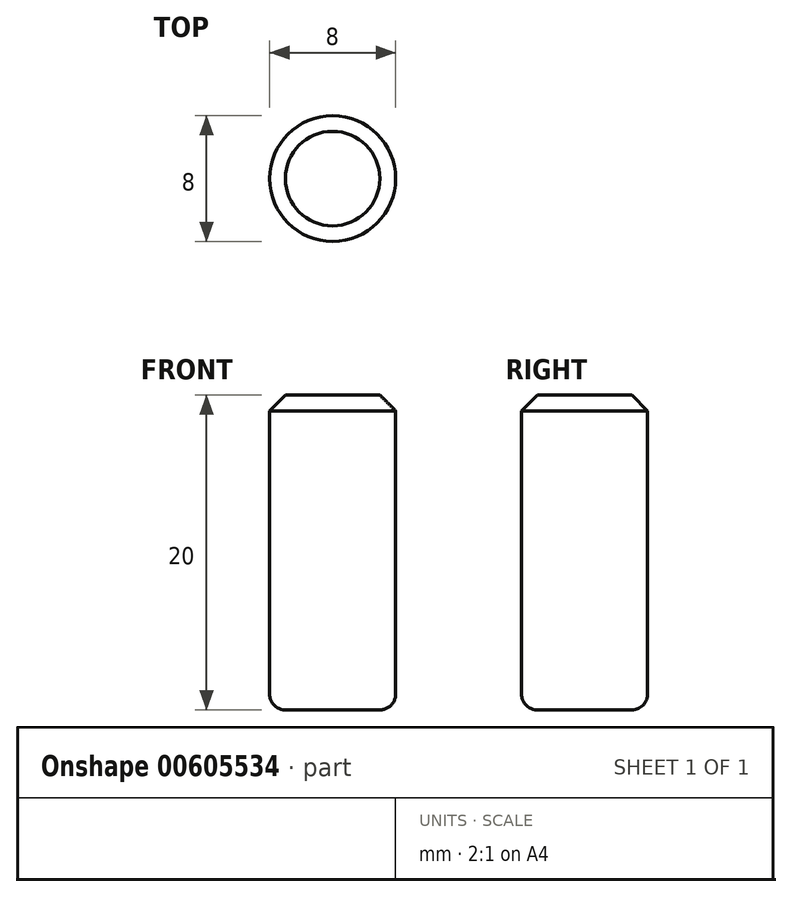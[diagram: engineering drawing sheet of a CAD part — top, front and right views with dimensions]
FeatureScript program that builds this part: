
annotation { "Feature Type Name" : "Feature", "Feature Type Description" : "" }
export const myFeature = defineFeature(function(context is Context, id is Id, definition is map)
    precondition{}
    {
        {
            var Q0;
            Q0=qCreatedBy(makeId("Top.planeOp"),FACE);
            var sketch = newSketch(context, id + "F0", { "sketchPlane" : qUnion([Q0])});
            skCircle(sketch, "E0", {"center": v(0, 0) * mm, "radius": 4 * mm});
            skSolve(sketch);
        }
        {
            var Q0;
            Q0=makeQuery(id+"F0.imprint","IMPRINT",FACE,{"disambiguationData":[TD([[makeQuery(id+"F0.imprint","IMPRINT",EDGE,{"derivedFrom":sQuery(id+"F0.wireOp",EDGE,"E0")}),1.0]])]});
            extrude(context, id + "F1", {"entities" : qUnion([Q0]), "oppositeDirection" : true, "depth" : 20 * mm, "offsetDistance" : 25 * mm});
        }
        {
            var Q0;
            Q0=makeQuery(id+"F1.opExtrude","CAP_EDGE",EDGE,{"disambiguationData":[OSD([sQuery(id+"F0.wireOp",EDGE,"E0")])],"isStart":false});
            fillet(context, id + "F2", {"entities" : qUnion([Q0]), "radius" : 1 * mm, "tangentPropagation" : true, "allowEdgeOverflow" : false});
        }
        {
            var Q0;
            Q0=makeQuery(id+"F1.opExtrude","CAP_EDGE",EDGE,{"disambiguationData":[OSD([sQuery(id+"F0.wireOp",EDGE,"E0")])],"isStart":true});
            chamfer(context, id + "F3", {"entities" : qUnion([Q0]), "width" : 1 * mm, "tangentPropagation" : true});
        }
    });
